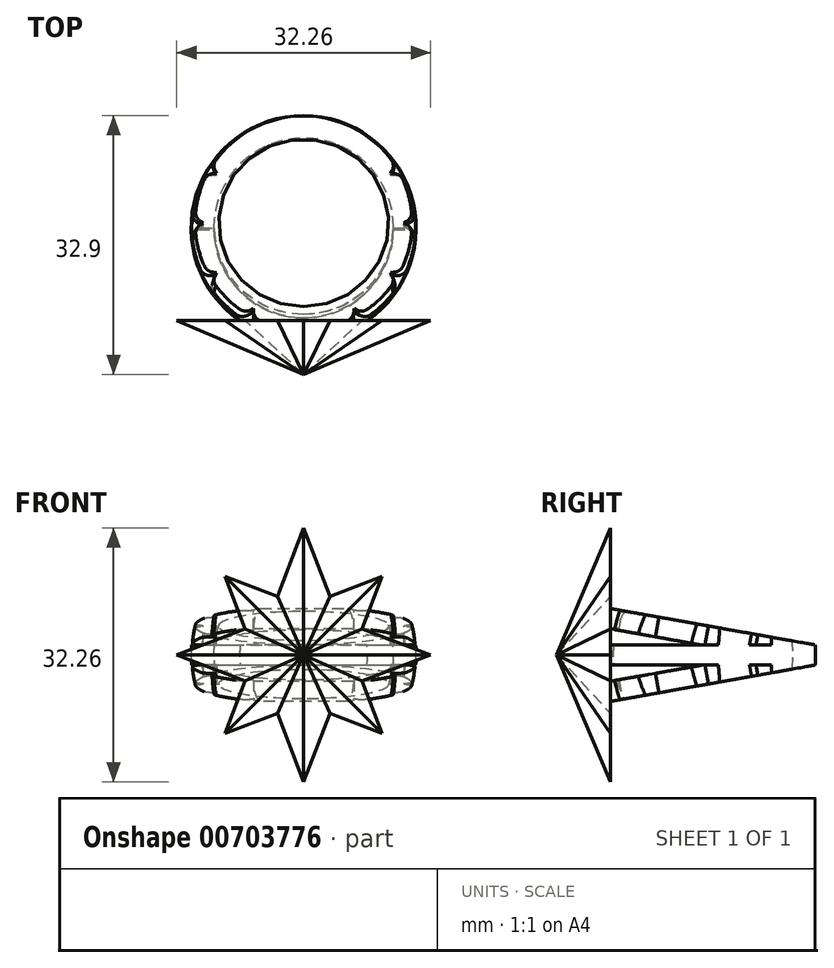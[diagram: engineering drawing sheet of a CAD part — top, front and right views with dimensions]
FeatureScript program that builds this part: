
annotation { "Feature Type Name" : "Feature", "Feature Type Description" : "" }
export const myFeature = defineFeature(function(context is Context, id is Id, definition is map)
    precondition{}
    {
        {
            var Q0;
            Q0=qCreatedBy(makeId("Right.planeOp"),FACE);
            var sketch = newSketch(context, id + "F0", { "sketchPlane" : qUnion([Q0])});
            skArc(sketch, "E0", {"start": v(0, -11.43) * mm, "mid": v(11.43, 0) * mm, "end": v(0, 11.43) * mm});
            skArc(sketch, "E1", {"start": v(0, -14.29) * mm, "mid": v(14.29, 0) * mm, "end": v(0, 14.29) * mm});
            skLineSegment(sketch, "E2", {"start": v(0, 11.43) * mm, "end": v(0, 14.29) * mm});
            skLineSegment(sketch, "E3", {"start": v(0, -14.29) * mm, "end": v(0, -11.43) * mm});
            skLineSegment(sketch, "E4", {"start": v(0, -11.43) * mm, "end": v(0, 11.43) * mm, "construction": true});
            skSolve(sketch);
        }
        {
            var Q0;
            Q0 = qSketchRegion(id + "F0", true);
            var Q1;
            Q1=sQuery(id+"F0.wireOp",EDGE,"E4");
            revolve(context, id + "F1", {"surfaceOperationType" : NewSurfaceOperationType.NEW, "entities" : qUnion([Q0]), "axis" : qUnion([Q1]), "revolveType" : RevolveType.FULL});
        }
        {
            var Q0;
            Q0=qCreatedBy(makeId("Right.planeOp"),FACE);
            var sketch = newSketch(context, id + "F2", { "sketchPlane" : qUnion([Q0])});
            skLineSegment(sketch, "E5", {"start": v(-14.29, -6.35) * mm, "end": v(-14.29, 6.35) * mm, "construction": true});
            skPoint(sketch, "E6", {"position": v(-14.29, 0) * mm});
            skLineSegment(sketch, "E7.bottom", {"start": v(-14.29, 1.27) * mm, "end": v(14.29, 1.27) * mm, "construction": true});
            skLineSegment(sketch, "E7.top", {"start": v(-14.29, -1.27) * mm, "end": v(14.29, -1.27) * mm, "construction": true});
            skLineSegment(sketch, "E7.left", {"start": v(-14.29, 1.27) * mm, "end": v(-14.29, -1.27) * mm, "construction": true});
            skLineSegment(sketch, "E7.right", {"start": v(14.29, 1.27) * mm, "end": v(14.29, -1.27) * mm, "construction": true});
            skPoint(sketch, "E8", {"position": v(14.29, 0) * mm});
            skLineSegment(sketch, "E9", {"start": v(14.29, 1.27) * mm, "end": v(-14.29, 6.35) * mm, "construction": true});
            skLineSegment(sketch, "E10", {"start": v(-14.29, 3.77) * mm, "end": v(14.29, -1.3) * mm, "construction": true});
            skLineSegment(sketch, "E11", {"start": v(-14.29, -6.35) * mm, "end": v(14.29, -1.3) * mm, "construction": true});
            skLineSegment(sketch, "E12", {"start": v(-14.29, -3.77) * mm, "end": v(14.29, 1.27) * mm, "construction": true});
            skSolve(sketch);
        }
        {
            var Q0;
            Q0=qCreatedBy(makeId("Right.planeOp"),FACE);
            var sketch = newSketch(context, id + "F3", { "sketchPlane" : qUnion([Q0])});
            skLineSegment(sketch, "E13", {"start": v(-14.29, -3.77) * mm, "end": v(0, -1.27) * mm});
            skLineSegment(sketch, "E14", {"start": v(0, -1.27) * mm, "end": v(-14.29, -1.27) * mm});
            skLineSegment(sketch, "E15", {"start": v(-14.29, -1.27) * mm, "end": v(-14.29, -3.77) * mm});
            skLineSegment(sketch, "E16", {"start": v(-14.29, 1.27) * mm, "end": v(-14.29, 3.77) * mm});
            skLineSegment(sketch, "E17", {"start": v(-14.29, 3.77) * mm, "end": v(0, 1.23) * mm});
            skLineSegment(sketch, "E18", {"start": v(0, 1.23) * mm, "end": v(-14.29, 1.27) * mm});
            skLineSegment(sketch, "E19", {"start": v(14.29, 1.27) * mm, "end": v(-14.29, 6.35) * mm});
            skLineSegment(sketch, "E20", {"start": v(-14.29, -6.35) * mm, "end": v(14.29, -1.27) * mm});
            skLineSegment(sketch, "E21", {"start": v(14.29, -1.27) * mm, "end": v(14.29, -16.1) * mm});
            skLineSegment(sketch, "E22", {"start": v(14.29, -16.1) * mm, "end": v(-14.29, -16.1) * mm});
            skLineSegment(sketch, "E23", {"start": v(-14.29, -16.1) * mm, "end": v(-14.29, -6.35) * mm});
            skLineSegment(sketch, "E24", {"start": v(-14.29, 16.15) * mm, "end": v(14.29, 16.15) * mm});
            skLineSegment(sketch, "E25", {"start": v(14.29, 16.15) * mm, "end": v(14.29, 1.27) * mm});
            skLineSegment(sketch, "E26", {"start": v(-14.29, 6.35) * mm, "end": v(-14.29, 16.15) * mm});
            skSolve(sketch);
        }
        {
            var Q0;
            Q0 = qSketchRegion(id + "F3", true);
            extrude(context, id + "F4", {"entities" : qUnion([Q0]), "operationType" : NewBodyOperationType.REMOVE, "oppositeDirection" : true, "depth" : 25.4 * mm, "offsetDistance" : 25.4 * mm, "hasSecondDirection" : true, "secondDirectionOppositeDirection" : false, "secondDirectionDepth" : 25.4 * mm});
        }
        {
            var Q0;
            Q0=makeQuery(id+"F4.boolean.opBoolean","COPY",FACE,{"derivedFrom":makeQuery(id+"F4.opExtrude","SWEPT_FACE",FACE,{"disambiguationData":[OSD([sQuery(id+"F3.wireOp",EDGE,"E19")])]})});
            var sketch = newSketch(context, id + "F5", { "sketchPlane" : qUnion([Q0])});
            skCircle(sketch, "E27", {"center": v(0, 0) * mm, "radius": 13.79 * mm, "construction": true});
            skLineSegment(sketch, "E28", {"start": v(0, -12.77) * mm, "end": v(-1.59, -15.31) * mm});
            skLineSegment(sketch, "E29", {"start": v(-1.59, -15.31) * mm, "end": v(1.59, -15.31) * mm});
            skLineSegment(sketch, "E30", {"start": v(1.59, -15.31) * mm, "end": v(0, -12.77) * mm});
            skPoint(sketch, "E31", {"position": v(0, -15.31) * mm});
            skLineSegment(sketch, "E32.1.0", {"start": v(6.28, -14.05) * mm, "end": v(9.03, -12.47) * mm});
            skLineSegment(sketch, "E32.1.1", {"start": v(9.03, -12.47) * mm, "end": v(6.39, -11.06) * mm});
            skLineSegment(sketch, "E32.1.2", {"start": v(6.39, -11.06) * mm, "end": v(6.28, -14.05) * mm});
            skLineSegment(sketch, "E32.2.0", {"start": v(12.47, -9.03) * mm, "end": v(14.05, -6.28) * mm});
            skLineSegment(sketch, "E32.2.1", {"start": v(14.05, -6.28) * mm, "end": v(11.06, -6.39) * mm});
            skLineSegment(sketch, "E32.2.2", {"start": v(11.06, -6.39) * mm, "end": v(12.47, -9.03) * mm});
            skLineSegment(sketch, "E32.3.0", {"start": v(15.31, -1.59) * mm, "end": v(15.31, 1.59) * mm});
            skLineSegment(sketch, "E32.3.1", {"start": v(15.31, 1.59) * mm, "end": v(12.77, 0) * mm});
            skLineSegment(sketch, "E32.3.2", {"start": v(12.77, 0) * mm, "end": v(15.31, -1.59) * mm});
            skLineSegment(sketch, "E32.4.0", {"start": v(14.05, 6.28) * mm, "end": v(12.47, 9.03) * mm});
            skLineSegment(sketch, "E32.4.1", {"start": v(12.47, 9.03) * mm, "end": v(11.06, 6.39) * mm});
            skLineSegment(sketch, "E32.4.2", {"start": v(11.06, 6.39) * mm, "end": v(14.05, 6.28) * mm});
            skLineSegment(sketch, "E32.8.0", {"start": v(-12.47, 9.03) * mm, "end": v(-14.05, 6.28) * mm});
            skLineSegment(sketch, "E32.8.1", {"start": v(-14.05, 6.28) * mm, "end": v(-11.06, 6.39) * mm});
            skLineSegment(sketch, "E32.8.2", {"start": v(-11.06, 6.39) * mm, "end": v(-12.47, 9.03) * mm});
            skLineSegment(sketch, "E32.9.0", {"start": v(-15.31, 1.59) * mm, "end": v(-15.31, -1.59) * mm});
            skLineSegment(sketch, "E32.9.1", {"start": v(-15.31, -1.59) * mm, "end": v(-12.77, 0) * mm});
            skLineSegment(sketch, "E32.9.2", {"start": v(-12.77, 0) * mm, "end": v(-15.31, 1.59) * mm});
            skLineSegment(sketch, "E32.10.0", {"start": v(-14.05, -6.28) * mm, "end": v(-12.47, -9.03) * mm});
            skLineSegment(sketch, "E32.10.1", {"start": v(-12.47, -9.03) * mm, "end": v(-11.06, -6.39) * mm});
            skLineSegment(sketch, "E32.10.2", {"start": v(-11.06, -6.39) * mm, "end": v(-14.05, -6.28) * mm});
            skLineSegment(sketch, "E32.11.0", {"start": v(-9.03, -12.47) * mm, "end": v(-6.28, -14.05) * mm});
            skLineSegment(sketch, "E32.11.1", {"start": v(-6.28, -14.05) * mm, "end": v(-6.39, -11.06) * mm});
            skLineSegment(sketch, "E32.11.2", {"start": v(-6.39, -11.06) * mm, "end": v(-9.03, -12.47) * mm});
            skSolve(sketch);
        }
        {
            var Q0;
            Q0 = qSketchRegion(id + "F5", true);
            extrude(context, id + "F6", {"entities" : qUnion([Q0]), "operationType" : NewBodyOperationType.REMOVE, "oppositeDirection" : true, "depth" : 2.54 * mm, "offsetDistance" : 25.4 * mm});
        }
        {
            var Q0;
            Q0=makeQuery(id+"F4.boolean.opBoolean","COPY",FACE,{"derivedFrom":makeQuery(id+"F4.opExtrude","SWEPT_FACE",FACE,{"disambiguationData":[OSD([sQuery(id+"F3.wireOp",EDGE,"E20")])]})});
            var sketch = newSketch(context, id + "F7", { "sketchPlane" : qUnion([Q0])});
            skLineSegment(sketch, "E33", {"start": v(0, 12.77) * mm, "end": v(-1.59, 15.31) * mm});
            skLineSegment(sketch, "E34", {"start": v(-1.59, 15.31) * mm, "end": v(1.59, 15.31) * mm});
            skLineSegment(sketch, "E35", {"start": v(1.59, 15.31) * mm, "end": v(0, 12.77) * mm});
            skPoint(sketch, "E36", {"position": v(0, 15.31) * mm});
            skCircle(sketch, "E37", {"center": v(0, 0) * mm, "radius": 13.79 * mm, "construction": true});
            skLineSegment(sketch, "E38.1.0", {"start": v(-9.03, 12.47) * mm, "end": v(-6.28, 14.05) * mm});
            skLineSegment(sketch, "E38.1.1", {"start": v(-6.28, 14.05) * mm, "end": v(-6.39, 11.06) * mm});
            skLineSegment(sketch, "E38.1.2", {"start": v(-6.39, 11.06) * mm, "end": v(-9.03, 12.47) * mm});
            skLineSegment(sketch, "E38.2.0", {"start": v(-14.05, 6.28) * mm, "end": v(-12.47, 9.03) * mm});
            skLineSegment(sketch, "E38.2.1", {"start": v(-12.47, 9.03) * mm, "end": v(-11.06, 6.39) * mm});
            skLineSegment(sketch, "E38.2.2", {"start": v(-11.06, 6.39) * mm, "end": v(-14.05, 6.28) * mm});
            skLineSegment(sketch, "E38.3.0", {"start": v(-15.31, -1.59) * mm, "end": v(-15.31, 1.59) * mm});
            skLineSegment(sketch, "E38.3.1", {"start": v(-15.31, 1.59) * mm, "end": v(-12.77, 0) * mm});
            skLineSegment(sketch, "E38.3.2", {"start": v(-12.77, 0) * mm, "end": v(-15.31, -1.59) * mm});
            skLineSegment(sketch, "E38.4.0", {"start": v(-12.47, -9.03) * mm, "end": v(-14.05, -6.28) * mm});
            skLineSegment(sketch, "E38.4.1", {"start": v(-14.05, -6.28) * mm, "end": v(-11.06, -6.39) * mm});
            skLineSegment(sketch, "E38.4.2", {"start": v(-11.06, -6.39) * mm, "end": v(-12.47, -9.03) * mm});
            skLineSegment(sketch, "E38.8.0", {"start": v(14.05, -6.28) * mm, "end": v(12.47, -9.03) * mm});
            skLineSegment(sketch, "E38.8.1", {"start": v(12.47, -9.03) * mm, "end": v(11.06, -6.39) * mm});
            skLineSegment(sketch, "E38.8.2", {"start": v(11.06, -6.39) * mm, "end": v(14.05, -6.28) * mm});
            skLineSegment(sketch, "E38.9.0", {"start": v(15.31, 1.59) * mm, "end": v(15.31, -1.59) * mm});
            skLineSegment(sketch, "E38.9.1", {"start": v(15.31, -1.59) * mm, "end": v(12.77, 0) * mm});
            skLineSegment(sketch, "E38.9.2", {"start": v(12.77, 0) * mm, "end": v(15.31, 1.59) * mm});
            skLineSegment(sketch, "E38.10.0", {"start": v(12.47, 9.03) * mm, "end": v(14.05, 6.28) * mm});
            skLineSegment(sketch, "E38.10.1", {"start": v(14.05, 6.28) * mm, "end": v(11.06, 6.39) * mm});
            skLineSegment(sketch, "E38.10.2", {"start": v(11.06, 6.39) * mm, "end": v(12.47, 9.03) * mm});
            skLineSegment(sketch, "E38.11.0", {"start": v(6.28, 14.05) * mm, "end": v(9.03, 12.47) * mm});
            skLineSegment(sketch, "E38.11.1", {"start": v(9.03, 12.47) * mm, "end": v(6.39, 11.06) * mm});
            skLineSegment(sketch, "E38.11.2", {"start": v(6.39, 11.06) * mm, "end": v(6.28, 14.05) * mm});
            skSolve(sketch);
        }
        {
            var Q0;
            Q0 = qSketchRegion(id + "F7", true);
            extrude(context, id + "F8", {"entities" : qUnion([Q0]), "operationType" : NewBodyOperationType.REMOVE, "oppositeDirection" : true, "depth" : 2.54 * mm, "offsetDistance" : 25.4 * mm});
        }
        {
            var Q0;
            Q0=qCreatedBy(makeId("Right.planeOp"),FACE);
            var sketch = newSketch(context, id + "F9", { "sketchPlane" : qUnion([Q0])});
            skArc(sketch, "E39", {"start": v(14.23, -1.27) * mm, "mid": v(14.29, 0) * mm, "end": v(14.23, 1.27) * mm});
            skLineSegment(sketch, "E40", {"start": v(14.23, 1.27) * mm, "end": v(11.36, 1.27) * mm});
            skLineSegment(sketch, "E41", {"start": v(14.23, -1.27) * mm, "end": v(11.36, -1.27) * mm});
            skArc(sketch, "E42", {"start": v(11.36, -1.27) * mm, "mid": v(11.43, 0) * mm, "end": v(11.36, 1.27) * mm});
            skLineSegment(sketch, "E43", {"start": v(0, 4.46) * mm, "end": v(0, -6.5) * mm, "construction": true});
            skSolve(sketch);
        }
        {
            var Q0;
            Q0 = qSketchRegion(id + "F9", true);
            var Q1;
            Q1=sQuery(id+"F9.wireOp",EDGE,"E43");
            revolve(context, id + "F10", {"operationType" : NewBodyOperationType.ADD, "surfaceOperationType" : NewSurfaceOperationType.NEW, "entities" : qUnion([Q0]), "axis" : qUnion([Q1]), "revolveType" : RevolveType.FULL});
        }
        {
            var Q0;
            Q0=makeQuery(id+"F8.boolean.opBoolean","INTERSECT",EDGE,{"derivedFrom":[makeQuery(id+"F6.boolean.opBoolean","SPLIT",FACE,{"disambiguationData":[TD([makeQuery(id+"F4.boolean.opBoolean","COPY",FACE,{"derivedFrom":makeQuery(id+"F4.opExtrude","SWEPT_FACE",FACE,{"disambiguationData":[OSD([sQuery(id+"F3.wireOp",EDGE,"E13")])]})})])],"derivedFrom":makeQuery(id+"F1.opRevolve","SWEPT_FACE",FACE,{"disambiguationData":[OSD([sQuery(id+"F0.wireOp",EDGE,"E1")])]})}),makeQuery(id+"F8.opExtrude","SWEPT_FACE",FACE,{"disambiguationData":[OSD([sQuery(id+"F7.wireOp",EDGE,"E33")])]})]});
            var Q1;
            Q1=makeQuery(id+"F8.boolean.opBoolean","INTERSECT",EDGE,{"derivedFrom":[makeQuery(id+"F6.boolean.opBoolean","SPLIT",FACE,{"disambiguationData":[TD([makeQuery(id+"F4.boolean.opBoolean","COPY",FACE,{"derivedFrom":makeQuery(id+"F4.opExtrude","SWEPT_FACE",FACE,{"disambiguationData":[OSD([sQuery(id+"F3.wireOp",EDGE,"E13")])]})})])],"derivedFrom":makeQuery(id+"F1.opRevolve","SWEPT_FACE",FACE,{"disambiguationData":[OSD([sQuery(id+"F0.wireOp",EDGE,"E1")])]})}),makeQuery(id+"F8.opExtrude","SWEPT_FACE",FACE,{"disambiguationData":[OSD([sQuery(id+"F7.wireOp",EDGE,"E38.1.1")])]})]});
            var Q2;
            Q2=makeQuery(id+"F8.boolean.opBoolean","INTERSECT",EDGE,{"derivedFrom":[makeQuery(id+"F6.boolean.opBoolean","SPLIT",FACE,{"disambiguationData":[TD([makeQuery(id+"F4.boolean.opBoolean","COPY",FACE,{"derivedFrom":makeQuery(id+"F4.opExtrude","SWEPT_FACE",FACE,{"disambiguationData":[OSD([sQuery(id+"F3.wireOp",EDGE,"E13")])]})})])],"derivedFrom":makeQuery(id+"F1.opRevolve","SWEPT_FACE",FACE,{"disambiguationData":[OSD([sQuery(id+"F0.wireOp",EDGE,"E1")])]})}),makeQuery(id+"F8.opExtrude","SWEPT_FACE",FACE,{"disambiguationData":[OSD([sQuery(id+"F7.wireOp",EDGE,"E38.1.2")])]})]});
            var Q3;
            Q3=makeQuery(id+"F8.boolean.opBoolean","INTERSECT",EDGE,{"derivedFrom":[makeQuery(id+"F6.boolean.opBoolean","SPLIT",FACE,{"disambiguationData":[TD([makeQuery(id+"F4.boolean.opBoolean","COPY",FACE,{"derivedFrom":makeQuery(id+"F4.opExtrude","SWEPT_FACE",FACE,{"disambiguationData":[OSD([sQuery(id+"F3.wireOp",EDGE,"E13")])]})})])],"derivedFrom":makeQuery(id+"F1.opRevolve","SWEPT_FACE",FACE,{"disambiguationData":[OSD([sQuery(id+"F0.wireOp",EDGE,"E1")])]})}),makeQuery(id+"F8.opExtrude","SWEPT_FACE",FACE,{"disambiguationData":[OSD([sQuery(id+"F7.wireOp",EDGE,"E38.2.1")])]})]});
            var Q4;
            Q4=makeQuery(id+"F8.boolean.opBoolean","INTERSECT",EDGE,{"derivedFrom":[makeQuery(id+"F6.boolean.opBoolean","SPLIT",FACE,{"disambiguationData":[TD([makeQuery(id+"F4.boolean.opBoolean","COPY",FACE,{"derivedFrom":makeQuery(id+"F4.opExtrude","SWEPT_FACE",FACE,{"disambiguationData":[OSD([sQuery(id+"F3.wireOp",EDGE,"E13")])]})})])],"derivedFrom":makeQuery(id+"F1.opRevolve","SWEPT_FACE",FACE,{"disambiguationData":[OSD([sQuery(id+"F0.wireOp",EDGE,"E1")])]})}),makeQuery(id+"F8.opExtrude","SWEPT_FACE",FACE,{"disambiguationData":[OSD([sQuery(id+"F7.wireOp",EDGE,"E38.2.2")])]})]});
            var Q5;
            Q5=makeQuery(id+"F8.boolean.opBoolean","INTERSECT",EDGE,{"derivedFrom":[makeQuery(id+"F6.boolean.opBoolean","SPLIT",FACE,{"disambiguationData":[TD([makeQuery(id+"F4.boolean.opBoolean","COPY",FACE,{"derivedFrom":makeQuery(id+"F4.opExtrude","SWEPT_FACE",FACE,{"disambiguationData":[OSD([sQuery(id+"F3.wireOp",EDGE,"E13")])]})})])],"derivedFrom":makeQuery(id+"F1.opRevolve","SWEPT_FACE",FACE,{"disambiguationData":[OSD([sQuery(id+"F0.wireOp",EDGE,"E1")])]})}),makeQuery(id+"F8.opExtrude","SWEPT_FACE",FACE,{"disambiguationData":[OSD([sQuery(id+"F7.wireOp",EDGE,"E38.3.1")])]})]});
            var Q6;
            Q6=makeQuery(id+"F8.boolean.opBoolean","INTERSECT",EDGE,{"derivedFrom":[makeQuery(id+"F6.boolean.opBoolean","SPLIT",FACE,{"disambiguationData":[TD([makeQuery(id+"F4.boolean.opBoolean","COPY",FACE,{"derivedFrom":makeQuery(id+"F4.opExtrude","SWEPT_FACE",FACE,{"disambiguationData":[OSD([sQuery(id+"F3.wireOp",EDGE,"E13")])]})})])],"derivedFrom":makeQuery(id+"F1.opRevolve","SWEPT_FACE",FACE,{"disambiguationData":[OSD([sQuery(id+"F0.wireOp",EDGE,"E1")])]})}),makeQuery(id+"F8.opExtrude","SWEPT_FACE",FACE,{"disambiguationData":[OSD([sQuery(id+"F7.wireOp",EDGE,"E38.3.2")])]})]});
            var Q7;
            Q7=makeQuery(id+"F8.boolean.opBoolean","INTERSECT",EDGE,{"derivedFrom":[makeQuery(id+"F6.boolean.opBoolean","SPLIT",FACE,{"disambiguationData":[TD([makeQuery(id+"F4.boolean.opBoolean","COPY",FACE,{"derivedFrom":makeQuery(id+"F4.opExtrude","SWEPT_FACE",FACE,{"disambiguationData":[OSD([sQuery(id+"F3.wireOp",EDGE,"E13")])]})})])],"derivedFrom":makeQuery(id+"F1.opRevolve","SWEPT_FACE",FACE,{"disambiguationData":[OSD([sQuery(id+"F0.wireOp",EDGE,"E1")])]})}),makeQuery(id+"F8.opExtrude","SWEPT_FACE",FACE,{"disambiguationData":[OSD([sQuery(id+"F7.wireOp",EDGE,"E35")])]})]});
            var Q8;
            Q8=makeQuery(id+"F8.boolean.opBoolean","INTERSECT",EDGE,{"derivedFrom":[makeQuery(id+"F6.boolean.opBoolean","SPLIT",FACE,{"disambiguationData":[TD([makeQuery(id+"F4.boolean.opBoolean","COPY",FACE,{"derivedFrom":makeQuery(id+"F4.opExtrude","SWEPT_FACE",FACE,{"disambiguationData":[OSD([sQuery(id+"F3.wireOp",EDGE,"E13")])]})})])],"derivedFrom":makeQuery(id+"F1.opRevolve","SWEPT_FACE",FACE,{"disambiguationData":[OSD([sQuery(id+"F0.wireOp",EDGE,"E1")])]})}),makeQuery(id+"F8.opExtrude","SWEPT_FACE",FACE,{"disambiguationData":[OSD([sQuery(id+"F7.wireOp",EDGE,"E38.11.2")])]})]});
            var Q9;
            Q9=makeQuery(id+"F8.boolean.opBoolean","INTERSECT",EDGE,{"derivedFrom":[makeQuery(id+"F6.boolean.opBoolean","SPLIT",FACE,{"disambiguationData":[TD([makeQuery(id+"F4.boolean.opBoolean","COPY",FACE,{"derivedFrom":makeQuery(id+"F4.opExtrude","SWEPT_FACE",FACE,{"disambiguationData":[OSD([sQuery(id+"F3.wireOp",EDGE,"E13")])]})})])],"derivedFrom":makeQuery(id+"F1.opRevolve","SWEPT_FACE",FACE,{"disambiguationData":[OSD([sQuery(id+"F0.wireOp",EDGE,"E1")])]})}),makeQuery(id+"F8.opExtrude","SWEPT_FACE",FACE,{"disambiguationData":[OSD([sQuery(id+"F7.wireOp",EDGE,"E38.11.1")])]})]});
            var Q10;
            Q10=makeQuery(id+"F8.boolean.opBoolean","INTERSECT",EDGE,{"derivedFrom":[makeQuery(id+"F6.boolean.opBoolean","SPLIT",FACE,{"disambiguationData":[TD([makeQuery(id+"F4.boolean.opBoolean","COPY",FACE,{"derivedFrom":makeQuery(id+"F4.opExtrude","SWEPT_FACE",FACE,{"disambiguationData":[OSD([sQuery(id+"F3.wireOp",EDGE,"E13")])]})})])],"derivedFrom":makeQuery(id+"F1.opRevolve","SWEPT_FACE",FACE,{"disambiguationData":[OSD([sQuery(id+"F0.wireOp",EDGE,"E1")])]})}),makeQuery(id+"F8.opExtrude","SWEPT_FACE",FACE,{"disambiguationData":[OSD([sQuery(id+"F7.wireOp",EDGE,"E38.10.2")])]})]});
            var Q11;
            Q11=makeQuery(id+"F8.boolean.opBoolean","INTERSECT",EDGE,{"derivedFrom":[makeQuery(id+"F6.boolean.opBoolean","SPLIT",FACE,{"disambiguationData":[TD([makeQuery(id+"F4.boolean.opBoolean","COPY",FACE,{"derivedFrom":makeQuery(id+"F4.opExtrude","SWEPT_FACE",FACE,{"disambiguationData":[OSD([sQuery(id+"F3.wireOp",EDGE,"E13")])]})})])],"derivedFrom":makeQuery(id+"F1.opRevolve","SWEPT_FACE",FACE,{"disambiguationData":[OSD([sQuery(id+"F0.wireOp",EDGE,"E1")])]})}),makeQuery(id+"F8.opExtrude","SWEPT_FACE",FACE,{"disambiguationData":[OSD([sQuery(id+"F7.wireOp",EDGE,"E38.10.1")])]})]});
            var Q12;
            Q12=makeQuery(id+"F8.boolean.opBoolean","INTERSECT",EDGE,{"derivedFrom":[makeQuery(id+"F6.boolean.opBoolean","SPLIT",FACE,{"disambiguationData":[TD([makeQuery(id+"F4.boolean.opBoolean","COPY",FACE,{"derivedFrom":makeQuery(id+"F4.opExtrude","SWEPT_FACE",FACE,{"disambiguationData":[OSD([sQuery(id+"F3.wireOp",EDGE,"E13")])]})})])],"derivedFrom":makeQuery(id+"F1.opRevolve","SWEPT_FACE",FACE,{"disambiguationData":[OSD([sQuery(id+"F0.wireOp",EDGE,"E1")])]})}),makeQuery(id+"F8.opExtrude","SWEPT_FACE",FACE,{"disambiguationData":[OSD([sQuery(id+"F7.wireOp",EDGE,"E38.9.2")])]})]});
            var Q13;
            Q13=makeQuery(id+"F8.boolean.opBoolean","INTERSECT",EDGE,{"derivedFrom":[makeQuery(id+"F6.boolean.opBoolean","SPLIT",FACE,{"disambiguationData":[TD([makeQuery(id+"F4.boolean.opBoolean","COPY",FACE,{"derivedFrom":makeQuery(id+"F4.opExtrude","SWEPT_FACE",FACE,{"disambiguationData":[OSD([sQuery(id+"F3.wireOp",EDGE,"E13")])]})})])],"derivedFrom":makeQuery(id+"F1.opRevolve","SWEPT_FACE",FACE,{"disambiguationData":[OSD([sQuery(id+"F0.wireOp",EDGE,"E1")])]})}),makeQuery(id+"F8.opExtrude","SWEPT_FACE",FACE,{"disambiguationData":[OSD([sQuery(id+"F7.wireOp",EDGE,"E38.9.1")])]})]});
            var Q14;
            Q14=makeQuery(id+"F8.boolean.opBoolean","INTERSECT",EDGE,{"derivedFrom":[makeQuery(id+"F6.boolean.opBoolean","SPLIT",FACE,{"disambiguationData":[TD([makeQuery(id+"F4.boolean.opBoolean","COPY",FACE,{"derivedFrom":makeQuery(id+"F4.opExtrude","SWEPT_FACE",FACE,{"disambiguationData":[OSD([sQuery(id+"F3.wireOp",EDGE,"E13")])]})})])],"derivedFrom":makeQuery(id+"F1.opRevolve","SWEPT_FACE",FACE,{"disambiguationData":[OSD([sQuery(id+"F0.wireOp",EDGE,"E1")])]})}),makeQuery(id+"F8.opExtrude","SWEPT_FACE",FACE,{"disambiguationData":[OSD([sQuery(id+"F7.wireOp",EDGE,"E38.8.2")])]})]});
            var Q15;
            Q15=makeQuery(id+"F8.boolean.opBoolean","INTERSECT",EDGE,{"derivedFrom":[makeQuery(id+"F6.boolean.opBoolean","SPLIT",FACE,{"disambiguationData":[TD([makeQuery(id+"F4.boolean.opBoolean","COPY",FACE,{"derivedFrom":makeQuery(id+"F4.opExtrude","SWEPT_FACE",FACE,{"disambiguationData":[OSD([sQuery(id+"F3.wireOp",EDGE,"E13")])]})})])],"derivedFrom":makeQuery(id+"F1.opRevolve","SWEPT_FACE",FACE,{"disambiguationData":[OSD([sQuery(id+"F0.wireOp",EDGE,"E1")])]})}),makeQuery(id+"F8.opExtrude","SWEPT_FACE",FACE,{"disambiguationData":[OSD([sQuery(id+"F7.wireOp",EDGE,"E38.8.1")])]})]});
            var Q16;
            Q16=makeQuery(id+"F8.boolean.opBoolean","INTERSECT",EDGE,{"derivedFrom":[makeQuery(id+"F6.boolean.opBoolean","SPLIT",FACE,{"disambiguationData":[TD([makeQuery(id+"F4.boolean.opBoolean","COPY",FACE,{"derivedFrom":makeQuery(id+"F4.opExtrude","SWEPT_FACE",FACE,{"disambiguationData":[OSD([sQuery(id+"F3.wireOp",EDGE,"E13")])]})})])],"derivedFrom":makeQuery(id+"F1.opRevolve","SWEPT_FACE",FACE,{"disambiguationData":[OSD([sQuery(id+"F0.wireOp",EDGE,"E1")])]})}),makeQuery(id+"F8.opExtrude","SWEPT_FACE",FACE,{"disambiguationData":[OSD([sQuery(id+"F7.wireOp",EDGE,"E38.4.2")])]})]});
            var Q17;
            Q17=makeQuery(id+"F8.boolean.opBoolean","INTERSECT",EDGE,{"derivedFrom":[makeQuery(id+"F6.boolean.opBoolean","SPLIT",FACE,{"disambiguationData":[TD([makeQuery(id+"F4.boolean.opBoolean","COPY",FACE,{"derivedFrom":makeQuery(id+"F4.opExtrude","SWEPT_FACE",FACE,{"disambiguationData":[OSD([sQuery(id+"F3.wireOp",EDGE,"E13")])]})})])],"derivedFrom":makeQuery(id+"F1.opRevolve","SWEPT_FACE",FACE,{"disambiguationData":[OSD([sQuery(id+"F0.wireOp",EDGE,"E1")])]})}),makeQuery(id+"F8.opExtrude","SWEPT_FACE",FACE,{"disambiguationData":[OSD([sQuery(id+"F7.wireOp",EDGE,"E38.4.1")])]})]});
            fillet(context, id + "F11", {"entities" : qUnion([Q0, Q1, Q2, Q3, Q4, Q5, Q6, Q7, Q8, Q9, Q10, Q11, Q12, Q13, Q14, Q15, Q16, Q17]), "radius" : 1.27 * mm, "tangentPropagation" : true, "allowEdgeOverflow" : false});
        }
        {
            var Q0;
            Q0=makeQuery(id+"F6.boolean.opBoolean","INTERSECT",EDGE,{"derivedFrom":[makeQuery(id+"F1.opRevolve","SWEPT_FACE",FACE,{"disambiguationData":[OSD([sQuery(id+"F0.wireOp",EDGE,"E1")])]}),makeQuery(id+"F6.opExtrude","SWEPT_FACE",FACE,{"disambiguationData":[OSD([sQuery(id+"F5.wireOp",EDGE,"E32.8.2")])]})]});
            var Q1;
            Q1=makeQuery(id+"F6.boolean.opBoolean","INTERSECT",EDGE,{"derivedFrom":[makeQuery(id+"F1.opRevolve","SWEPT_FACE",FACE,{"disambiguationData":[OSD([sQuery(id+"F0.wireOp",EDGE,"E1")])]}),makeQuery(id+"F6.opExtrude","SWEPT_FACE",FACE,{"disambiguationData":[OSD([sQuery(id+"F5.wireOp",EDGE,"E32.8.1")])]})]});
            var Q2;
            Q2=makeQuery(id+"F6.boolean.opBoolean","INTERSECT",EDGE,{"derivedFrom":[makeQuery(id+"F1.opRevolve","SWEPT_FACE",FACE,{"disambiguationData":[OSD([sQuery(id+"F0.wireOp",EDGE,"E1")])]}),makeQuery(id+"F6.opExtrude","SWEPT_FACE",FACE,{"disambiguationData":[OSD([sQuery(id+"F5.wireOp",EDGE,"E32.9.2")])]})]});
            var Q3;
            Q3=makeQuery(id+"F6.boolean.opBoolean","INTERSECT",EDGE,{"derivedFrom":[makeQuery(id+"F1.opRevolve","SWEPT_FACE",FACE,{"disambiguationData":[OSD([sQuery(id+"F0.wireOp",EDGE,"E1")])]}),makeQuery(id+"F6.opExtrude","SWEPT_FACE",FACE,{"disambiguationData":[OSD([sQuery(id+"F5.wireOp",EDGE,"E32.9.1")])]})]});
            var Q4;
            Q4=makeQuery(id+"F6.boolean.opBoolean","INTERSECT",EDGE,{"derivedFrom":[makeQuery(id+"F1.opRevolve","SWEPT_FACE",FACE,{"disambiguationData":[OSD([sQuery(id+"F0.wireOp",EDGE,"E1")])]}),makeQuery(id+"F6.opExtrude","SWEPT_FACE",FACE,{"disambiguationData":[OSD([sQuery(id+"F5.wireOp",EDGE,"E32.10.2")])]})]});
            var Q5;
            Q5=makeQuery(id+"F6.boolean.opBoolean","INTERSECT",EDGE,{"derivedFrom":[makeQuery(id+"F1.opRevolve","SWEPT_FACE",FACE,{"disambiguationData":[OSD([sQuery(id+"F0.wireOp",EDGE,"E1")])]}),makeQuery(id+"F6.opExtrude","SWEPT_FACE",FACE,{"disambiguationData":[OSD([sQuery(id+"F5.wireOp",EDGE,"E32.10.1")])]})]});
            var Q6;
            Q6=makeQuery(id+"F6.boolean.opBoolean","INTERSECT",EDGE,{"derivedFrom":[makeQuery(id+"F1.opRevolve","SWEPT_FACE",FACE,{"disambiguationData":[OSD([sQuery(id+"F0.wireOp",EDGE,"E1")])]}),makeQuery(id+"F6.opExtrude","SWEPT_FACE",FACE,{"disambiguationData":[OSD([sQuery(id+"F5.wireOp",EDGE,"E32.11.2")])]})]});
            var Q7;
            Q7=makeQuery(id+"F6.boolean.opBoolean","INTERSECT",EDGE,{"derivedFrom":[makeQuery(id+"F1.opRevolve","SWEPT_FACE",FACE,{"disambiguationData":[OSD([sQuery(id+"F0.wireOp",EDGE,"E1")])]}),makeQuery(id+"F6.opExtrude","SWEPT_FACE",FACE,{"disambiguationData":[OSD([sQuery(id+"F5.wireOp",EDGE,"E32.11.1")])]})]});
            var Q8;
            Q8=makeQuery(id+"F6.boolean.opBoolean","INTERSECT",EDGE,{"derivedFrom":[makeQuery(id+"F1.opRevolve","SWEPT_FACE",FACE,{"disambiguationData":[OSD([sQuery(id+"F0.wireOp",EDGE,"E1")])]}),makeQuery(id+"F6.opExtrude","SWEPT_FACE",FACE,{"disambiguationData":[OSD([sQuery(id+"F5.wireOp",EDGE,"E28")])]})]});
            var Q9;
            Q9=makeQuery(id+"F6.boolean.opBoolean","INTERSECT",EDGE,{"derivedFrom":[makeQuery(id+"F1.opRevolve","SWEPT_FACE",FACE,{"disambiguationData":[OSD([sQuery(id+"F0.wireOp",EDGE,"E1")])]}),makeQuery(id+"F6.opExtrude","SWEPT_FACE",FACE,{"disambiguationData":[OSD([sQuery(id+"F5.wireOp",EDGE,"E30")])]})]});
            var Q10;
            Q10=makeQuery(id+"F6.boolean.opBoolean","INTERSECT",EDGE,{"derivedFrom":[makeQuery(id+"F1.opRevolve","SWEPT_FACE",FACE,{"disambiguationData":[OSD([sQuery(id+"F0.wireOp",EDGE,"E1")])]}),makeQuery(id+"F6.opExtrude","SWEPT_FACE",FACE,{"disambiguationData":[OSD([sQuery(id+"F5.wireOp",EDGE,"E32.1.2")])]})]});
            var Q11;
            Q11=makeQuery(id+"F6.boolean.opBoolean","INTERSECT",EDGE,{"derivedFrom":[makeQuery(id+"F1.opRevolve","SWEPT_FACE",FACE,{"disambiguationData":[OSD([sQuery(id+"F0.wireOp",EDGE,"E1")])]}),makeQuery(id+"F6.opExtrude","SWEPT_FACE",FACE,{"disambiguationData":[OSD([sQuery(id+"F5.wireOp",EDGE,"E32.1.1")])]})]});
            var Q12;
            Q12=makeQuery(id+"F6.boolean.opBoolean","INTERSECT",EDGE,{"derivedFrom":[makeQuery(id+"F1.opRevolve","SWEPT_FACE",FACE,{"disambiguationData":[OSD([sQuery(id+"F0.wireOp",EDGE,"E1")])]}),makeQuery(id+"F6.opExtrude","SWEPT_FACE",FACE,{"disambiguationData":[OSD([sQuery(id+"F5.wireOp",EDGE,"E32.2.2")])]})]});
            var Q13;
            Q13=makeQuery(id+"F6.boolean.opBoolean","INTERSECT",EDGE,{"derivedFrom":[makeQuery(id+"F1.opRevolve","SWEPT_FACE",FACE,{"disambiguationData":[OSD([sQuery(id+"F0.wireOp",EDGE,"E1")])]}),makeQuery(id+"F6.opExtrude","SWEPT_FACE",FACE,{"disambiguationData":[OSD([sQuery(id+"F5.wireOp",EDGE,"E32.2.1")])]})]});
            var Q14;
            Q14=makeQuery(id+"F6.boolean.opBoolean","INTERSECT",EDGE,{"derivedFrom":[makeQuery(id+"F1.opRevolve","SWEPT_FACE",FACE,{"disambiguationData":[OSD([sQuery(id+"F0.wireOp",EDGE,"E1")])]}),makeQuery(id+"F6.opExtrude","SWEPT_FACE",FACE,{"disambiguationData":[OSD([sQuery(id+"F5.wireOp",EDGE,"E32.3.2")])]})]});
            var Q15;
            Q15=makeQuery(id+"F6.boolean.opBoolean","INTERSECT",EDGE,{"derivedFrom":[makeQuery(id+"F1.opRevolve","SWEPT_FACE",FACE,{"disambiguationData":[OSD([sQuery(id+"F0.wireOp",EDGE,"E1")])]}),makeQuery(id+"F6.opExtrude","SWEPT_FACE",FACE,{"disambiguationData":[OSD([sQuery(id+"F5.wireOp",EDGE,"E32.3.1")])]})]});
            var Q16;
            Q16=makeQuery(id+"F6.boolean.opBoolean","INTERSECT",EDGE,{"derivedFrom":[makeQuery(id+"F1.opRevolve","SWEPT_FACE",FACE,{"disambiguationData":[OSD([sQuery(id+"F0.wireOp",EDGE,"E1")])]}),makeQuery(id+"F6.opExtrude","SWEPT_FACE",FACE,{"disambiguationData":[OSD([sQuery(id+"F5.wireOp",EDGE,"E32.4.1")])]})]});
            var Q17;
            Q17=makeQuery(id+"F6.boolean.opBoolean","INTERSECT",EDGE,{"derivedFrom":[makeQuery(id+"F1.opRevolve","SWEPT_FACE",FACE,{"disambiguationData":[OSD([sQuery(id+"F0.wireOp",EDGE,"E1")])]}),makeQuery(id+"F6.opExtrude","SWEPT_FACE",FACE,{"disambiguationData":[OSD([sQuery(id+"F5.wireOp",EDGE,"E32.4.2")])]})]});
            fillet(context, id + "F12", {"entities" : qUnion([Q0, Q1, Q2, Q3, Q4, Q5, Q6, Q7, Q8, Q9, Q10, Q11, Q12, Q13, Q14, Q15, Q16, Q17]), "radius" : 1.27 * mm, "tangentPropagation" : true, "allowEdgeOverflow" : false});
        }
        {
            var Q0;
            Q0=qCreatedBy(makeId("Front.planeOp"),FACE);
            cPlane(context, id + "F13", {"entities" : qUnion([Q0]), "cplaneType" : CPlaneType.OFFSET, "offset" : 14.29 * mm, "width" : 152.4 * mm, "height" : 152.4 * mm});
        }
        {
            var Q0;
            Q0=qCreatedBy(id+"F13.planeOp",FACE);
            var sketch = newSketch(context, id + "F14", { "sketchPlane" : qUnion([Q0])});
            skCircle(sketch, "E44.cCircle", {"center": v(0, 0) * mm, "radius": 8.9 * mm, "construction": true});
            skLineSegment(sketch, "E44.0", {"start": v(6.29, -6.29) * mm, "end": v(-6.29, -6.29) * mm, "construction": true});
            skLineSegment(sketch, "E44.1", {"start": v(-6.29, -6.29) * mm, "end": v(-6.29, 6.29) * mm, "construction": true});
            skLineSegment(sketch, "E44.2", {"start": v(-6.29, 6.29) * mm, "end": v(6.29, 6.29) * mm, "construction": true});
            skLineSegment(sketch, "E44.3", {"start": v(6.29, 6.29) * mm, "end": v(6.29, -6.29) * mm, "construction": true});
            skCircle(sketch, "E45.cCircle", {"center": v(0, 0) * mm, "radius": 10.16 * mm, "construction": true});
            skLineSegment(sketch, "E45.0", {"start": v(0, -10.16) * mm, "end": v(-10.16, 0) * mm, "construction": true});
            skLineSegment(sketch, "E45.1", {"start": v(-10.16, 0) * mm, "end": v(0, 10.16) * mm, "construction": true});
            skLineSegment(sketch, "E45.2", {"start": v(0, 10.16) * mm, "end": v(10.16, 0) * mm, "construction": true});
            skLineSegment(sketch, "E45.3", {"start": v(10.16, 0) * mm, "end": v(0, -10.16) * mm, "construction": true});
            skSolve(sketch);
        }
        {
            var Q0;
            Q0=qCreatedBy(id+"F13.planeOp",FACE);
            var sketch = newSketch(context, id + "F15", { "sketchPlane" : qUnion([Q0])});
            skLineSegment(sketch, "E46", {"start": v(0, 10.16) * mm, "end": v(-6.29, -6.29) * mm, "construction": true});
            skLineSegment(sketch, "E47", {"start": v(0, 10.16) * mm, "end": v(6.29, -6.29) * mm, "construction": true});
            skLineSegment(sketch, "E48", {"start": v(6.29, -6.29) * mm, "end": v(-10.16, 0) * mm, "construction": true});
            skLineSegment(sketch, "E49", {"start": v(-10.16, 0) * mm, "end": v(6.29, 6.29) * mm, "construction": true});
            skLineSegment(sketch, "E50", {"start": v(6.29, 6.29) * mm, "end": v(0, -10.16) * mm, "construction": true});
            skLineSegment(sketch, "E51", {"start": v(0, -10.16) * mm, "end": v(-6.29, 6.29) * mm, "construction": true});
            skLineSegment(sketch, "E52", {"start": v(-6.29, 6.29) * mm, "end": v(10.16, 0) * mm, "construction": true});
            skLineSegment(sketch, "E53", {"start": v(10.16, 0) * mm, "end": v(-6.29, -6.29) * mm, "construction": true});
            skSolve(sketch);
        }
        {
            var Q0;
            Q0=qCreatedBy(id+"F13.planeOp",FACE);
            var sketch = newSketch(context, id + "F16", { "sketchPlane" : qUnion([Q0])});
            skLineSegment(sketch, "E54", {"start": v(-6.29, -6.29) * mm, "end": v(-4.68, -2.1) * mm});
            skLineSegment(sketch, "E55", {"start": v(-4.68, -2.1) * mm, "end": v(-10.16, 0) * mm});
            skLineSegment(sketch, "E56", {"start": v(-10.16, 0) * mm, "end": v(-4.68, 2.1) * mm});
            skLineSegment(sketch, "E57", {"start": v(-4.68, 2.1) * mm, "end": v(-6.29, 6.29) * mm});
            skLineSegment(sketch, "E58", {"start": v(-6.29, 6.29) * mm, "end": v(-2.1, 4.68) * mm});
            skLineSegment(sketch, "E59", {"start": v(-2.1, 4.68) * mm, "end": v(0, 10.16) * mm});
            skLineSegment(sketch, "E60", {"start": v(0, 10.16) * mm, "end": v(2.1, 4.68) * mm});
            skLineSegment(sketch, "E61", {"start": v(2.1, 4.68) * mm, "end": v(6.29, 6.29) * mm});
            skLineSegment(sketch, "E62", {"start": v(6.29, 6.29) * mm, "end": v(4.68, 2.1) * mm});
            skLineSegment(sketch, "E63", {"start": v(4.68, 2.1) * mm, "end": v(10.16, 0) * mm});
            skLineSegment(sketch, "E64", {"start": v(10.16, 0) * mm, "end": v(4.68, -2.1) * mm});
            skLineSegment(sketch, "E65", {"start": v(4.68, -2.1) * mm, "end": v(6.29, -6.29) * mm});
            skLineSegment(sketch, "E66", {"start": v(6.29, -6.29) * mm, "end": v(2.1, -4.68) * mm});
            skLineSegment(sketch, "E67", {"start": v(2.1, -4.68) * mm, "end": v(0, -10.16) * mm});
            skLineSegment(sketch, "E68", {"start": v(0, -10.16) * mm, "end": v(-2.1, -4.68) * mm});
            skLineSegment(sketch, "E69", {"start": v(-2.1, -4.68) * mm, "end": v(-6.29, -6.29) * mm});
            skSolve(sketch);
        }
        {
            var Q0;
            Q0 = qSketchRegion(id + "F16", true);
            extrude(context, id + "F17", {"entities" : qUnion([Q0]), "operationType" : NewBodyOperationType.ADD, "depth" : 4.44 * mm, "offsetDistance" : 25.4 * mm, "hasDraft" : true, "draftAngle" : 40 * degree, "draftPullDirection" : true, "hasSecondDirection" : true, "secondDirectionOppositeDirection" : true, "secondDirectionDepth" : 2.54 * mm, "hasSecondDirectionDraft" : true, "secondDirectionDraftAngle" : 40 * degree});
        }
    });
